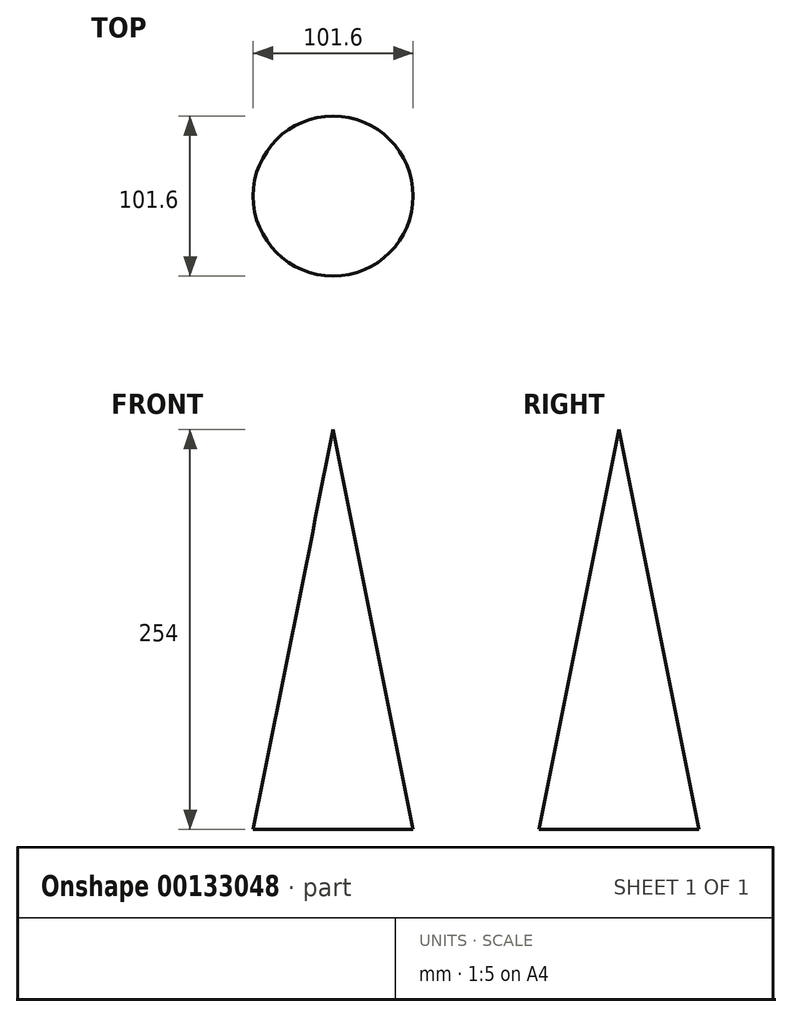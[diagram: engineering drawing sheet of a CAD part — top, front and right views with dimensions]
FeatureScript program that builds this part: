
annotation { "Feature Type Name" : "Feature", "Feature Type Description" : "" }
export const myFeature = defineFeature(function(context is Context, id is Id, definition is map)
    precondition{}
    {
        {
            var Q0;
            Q0=qCreatedBy(makeId("Front.planeOp"),FACE);
            var sketch = newSketch(context, id + "F0", { "sketchPlane" : qUnion([Q0])});
            skLineSegment(sketch, "E0", {"start": v(0, 0) * mm, "end": v(0, 254) * mm});
            skLineSegment(sketch, "E1", {"start": v(0, 0) * mm, "end": v(50.8, 0) * mm});
            skLineSegment(sketch, "E2", {"start": v(0, 254) * mm, "end": v(50.8, 0) * mm});
            skSolve(sketch);
        }
        {
            var Q0;
            Q0 = qSketchRegion(id + "F0", true);
            var Q1;
            Q1=sQuery(id+"F0.wireOp",EDGE,"E0");
            revolve(context, id + "F1", {"entities" : qUnion([Q0]), "axis" : qUnion([Q1]), "revolveType" : RevolveType.FULL});
        }
    });
